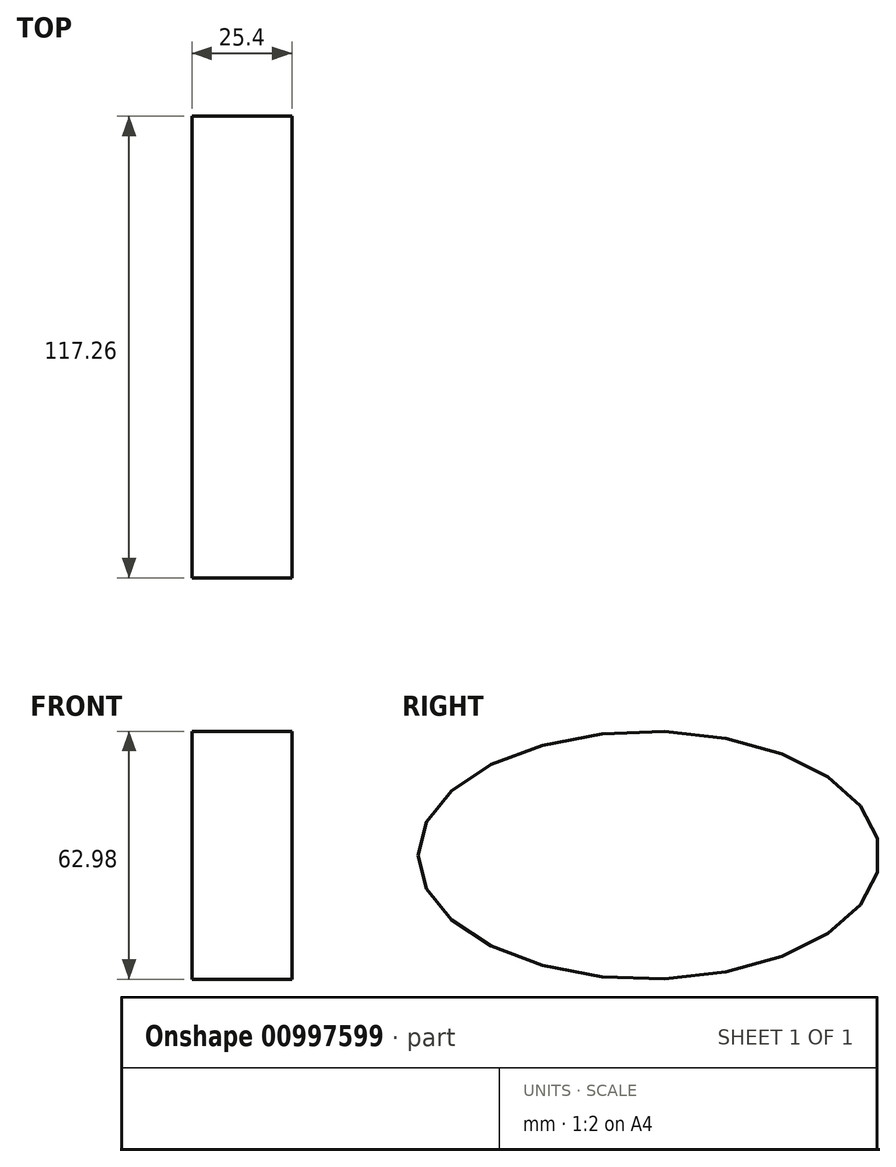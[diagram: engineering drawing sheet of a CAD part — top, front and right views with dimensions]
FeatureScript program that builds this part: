
annotation { "Feature Type Name" : "Feature", "Feature Type Description" : "" }
export const myFeature = defineFeature(function(context is Context, id is Id, definition is map)
    precondition{}
    {
        {
            var Q0;
            Q0=qCreatedBy(makeId("Right.planeOp"),FACE);
            var sketch = newSketch(context, id + "F0", { "sketchPlane" : qUnion([Q0])});
            skEllipse(sketch, "E0", {"center": v(0, 0) * mm, "majorRadius": 58.63 * mm, "minorRadius": 31.5 * mm, "majorAxis": v(-1, 0)});
            skSolve(sketch);
        }
        {
            var Q0;
            Q0=makeQuery(id+"F0.imprint","IMPRINT",FACE,{"disambiguationData":[TD([[makeQuery(id+"F0.imprint","IMPRINT",EDGE,{"derivedFrom":sQuery(id+"F0.wireOp",EDGE,"E0")}),1.0]])]});
            extrude(context, id + "F1", {"entities" : qUnion([Q0]), "depth" : 25.4 * mm, "offsetDistance" : 25.4 * mm});
        }
    });
